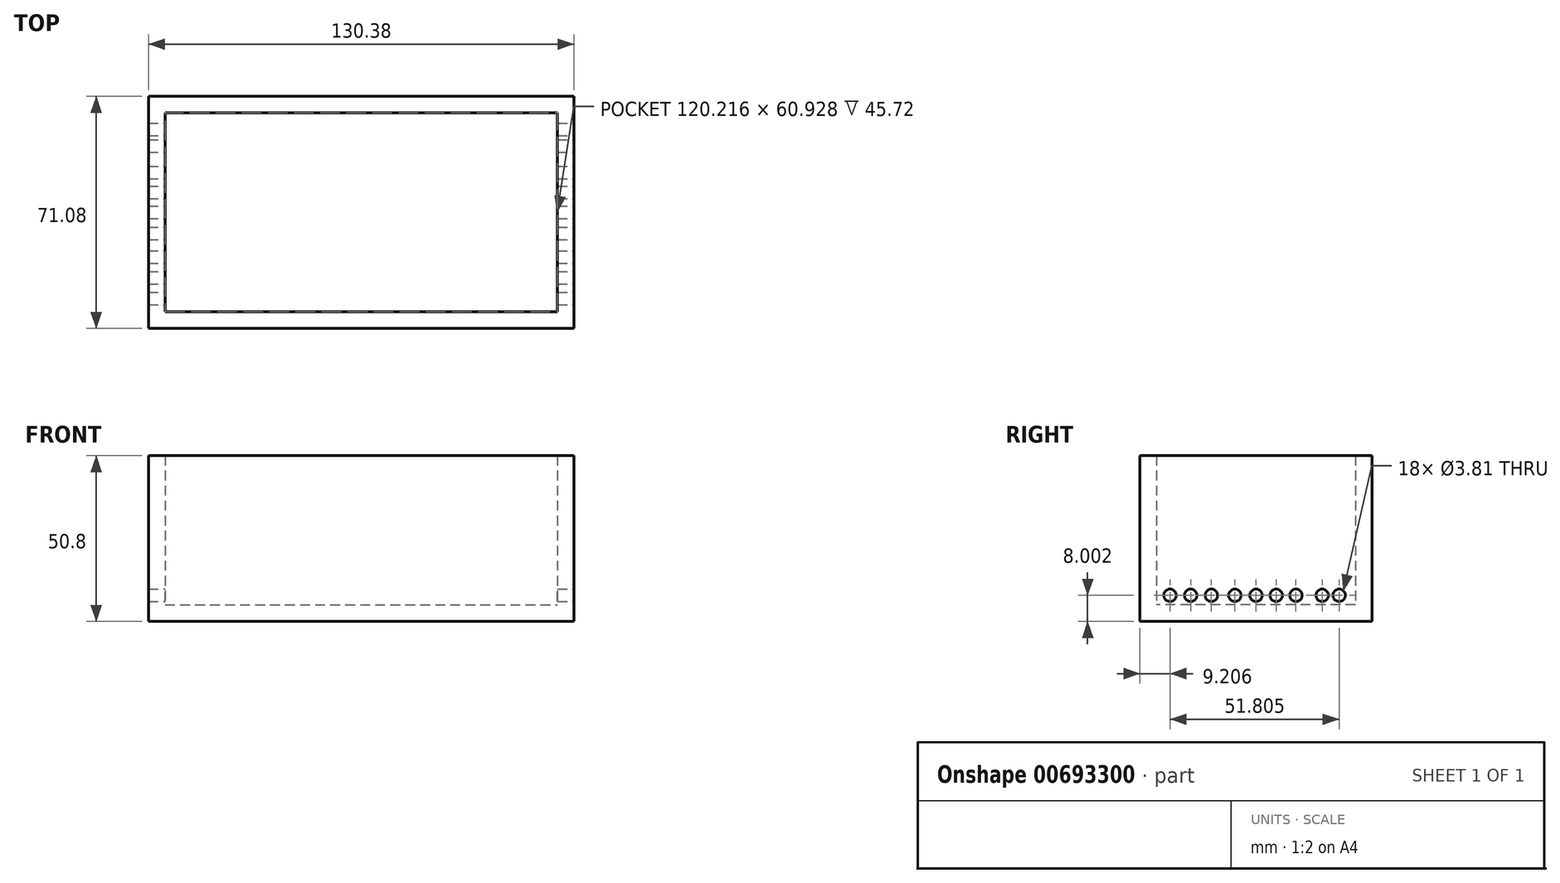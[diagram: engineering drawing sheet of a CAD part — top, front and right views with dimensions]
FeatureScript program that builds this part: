
annotation { "Feature Type Name" : "Feature", "Feature Type Description" : "" }
export const myFeature = defineFeature(function(context is Context, id is Id, definition is map)
    precondition{}
    {
        {
            var Q0;
            Q0=qCreatedBy(makeId("Top.planeOp"),FACE);
            var sketch = newSketch(context, id + "F0", { "sketchPlane" : qUnion([Q0])});
            skLineSegment(sketch, "E0.bottom", {"start": v(-65.19, 35.54) * mm, "end": v(65.19, 35.54) * mm});
            skLineSegment(sketch, "E0.top", {"start": v(-65.19, -35.54) * mm, "end": v(65.19, -35.54) * mm});
            skLineSegment(sketch, "E0.left", {"start": v(-65.19, 35.54) * mm, "end": v(-65.19, -35.54) * mm});
            skLineSegment(sketch, "E0.right", {"start": v(65.19, 35.54) * mm, "end": v(65.19, -35.54) * mm});
            skPoint(sketch, "E0.middle", {"position": v(0, 0) * mm});
            skSolve(sketch);
        }
        {
            var Q0;
            Q0=makeQuery(id+"F0.imprint","IMPRINT",FACE,{"disambiguationData":[TD([[makeQuery(id+"F0.imprint","IMPRINT",EDGE,{"derivedFrom":sQuery(id+"F0.wireOp",EDGE,"E0.bottom")}),-1.0]])]});
            extrude(context, id + "F1", {"entities" : qUnion([Q0]), "depth" : 50.8 * mm, "offsetDistance" : 25.4 * mm});
        }
        {
            var Q0;
            Q0=makeQuery(id+"F1.opExtrude","CAP_FACE",FACE,{"disambiguationData":[OSD([sQuery(id+"F0.wireOp",EDGE,"E0.bottom"),sQuery(id+"F0.wireOp",EDGE,"E0.top"),sQuery(id+"F0.wireOp",EDGE,"E0.left"),sQuery(id+"F0.wireOp",EDGE,"E0.right")])],"isStart":false});
            shell(context, id + "F2", {"entities" : qUnion([Q0]), "thickness" : 5.08 * mm});
        }
        {
            var Q0;
            Q0=makeQuery(id+"F1.opExtrude","SWEPT_FACE",FACE,{"disambiguationData":[OSD([sQuery(id+"F0.wireOp",EDGE,"E0.right")])]});
            var sketch = newSketch(context, id + "F3", { "sketchPlane" : qUnion([Q0])});
            skPoint(sketch, "E1", {"position": v(0, 8) * mm});
            skPoint(sketch, "E2", {"position": v(-6.48, 8) * mm});
            skPoint(sketch, "E3", {"position": v(-13.67, 8) * mm});
            skPoint(sketch, "E4", {"position": v(-20, 8) * mm});
            skPoint(sketch, "E5", {"position": v(-26.33, 8) * mm});
            skPoint(sketch, "E6", {"position": v(6.19, 8) * mm});
            skPoint(sketch, "E7", {"position": v(12.23, 8) * mm});
            skPoint(sketch, "E8", {"position": v(20.3, 8) * mm});
            skPoint(sketch, "E9", {"position": v(25.47, 8) * mm});
            skSolve(sketch);
        }
        {
            var Q0;
            Q0=sQuery(id+"F3.wireOp",VERTEX,"E5");
            var Q1;
            Q1=sQuery(id+"F3.wireOp",VERTEX,"E4");
            var Q2;
            Q2=sQuery(id+"F3.wireOp",VERTEX,"E3");
            var Q3;
            Q3=sQuery(id+"F3.wireOp",VERTEX,"E2");
            var Q4;
            Q4=sQuery(id+"F3.wireOp",VERTEX,"E1");
            var Q5;
            Q5=sQuery(id+"F3.wireOp",VERTEX,"E6");
            var Q6;
            Q6=sQuery(id+"F3.wireOp",VERTEX,"E7");
            var Q7;
            Q7=sQuery(id+"F3.wireOp",VERTEX,"E8");
            var Q8;
            Q8=sQuery(id+"F3.wireOp",VERTEX,"E9");
            var Q9;
            Q9=makeQuery(id+"F1.opExtrude","SWEPT_BODY",BODY,{"disambiguationData":[OSD([sQuery(id+"F0.wireOp",EDGE,"E0.bottom"),sQuery(id+"F0.wireOp",EDGE,"E0.top"),sQuery(id+"F0.wireOp",EDGE,"E0.left"),sQuery(id+"F0.wireOp",EDGE,"E0.right")])]});
            hole(context, id + "F4", {"style" : HoleStyle.SIMPLE, "endStyle" : HoleEndStyle.THROUGH, "holeDiameter" : 3.8 * mm, "majorDiameter" : 6.35 * mm, "isTappedThrough" : true, "tappedDepth" : 12.7 * mm, "tapClearance" : 3, "locations" : qUnion([Q0, Q1, Q2, Q3, Q4, Q5, Q6, Q7, Q8]), "scope" : qUnion([Q9])});
        }
    });
